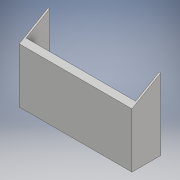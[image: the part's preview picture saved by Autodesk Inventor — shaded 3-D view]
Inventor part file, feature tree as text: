
AUTODESK INVENTOR PART (.ipt)
format: ipt  version: 2018.2 (Build 222227000, 227)  size: 170,496 bytes
history: native  units: mm
features: extrude x8, sketch x6
ambient origin geometry x8: Origin, YZ Plane, XZ Plane, XY Plane, X Axis, Y Axis, Z Axis, Center Point
bodies: Body1 (feature_tree)
feature tree (14):
  extrude  "Extrusion5"  Depth=160.0mm
  extrude  "Extrusion6"  Depth=38.5mm
  extrude  "Extrusion7"  Depth=155.2mm TaperAngle=0.0deg
  extrude  "Extrusion8"  TaperAngle=120.0deg  [1 undecoded]
  extrude  "Extrusion9"  Depth=2.4mm TaperAngle=0.0deg
  extrude  "Extrusion10"  Depth=2.4mm TaperAngle=0.0deg
  extrude  "Extrusion11"  Depth=6.0mm
  extrude  "Extrusion12"  Depth=2.4mm
  sketch  "Sketch6"  dims[d0=40.9mm d1=160.0mm]
  sketch  "Sketch7"  dims[d2=2.4mm d3=38.5mm]
  sketch  "Sketch8"  dims[d4=155.2mm d17=77.7mm d18=0.0mm]
  sketch  "Sketch9"  dims[d19=10.0mm d20=0.0mm d21=120.0deg]
  sketch  "Sketch10"  dims[d22=2.4mm d23=0.0mm d24=2.4mm d25=0.0mm]
  sketch  "Sketch11"  dims[d26=2.4mm d27=157.0mm d28=0.0mm d29=6.0mm d30=2.4mm d31=6.0mm d32=90.0deg d33=2.4mm d34=6.0mm d35=60.0deg d36=120.0deg d37=157.0mm d38=0.0mm d39=60.0deg d40=2.4mm d41=0.0mm d42=2.4mm d43=0.0mm]
note: 1 required parameter value undecoded (feature->parameter linkage not recoverable at this tier; creation-order binding heuristic only, values carry confidence <= 0.55)
